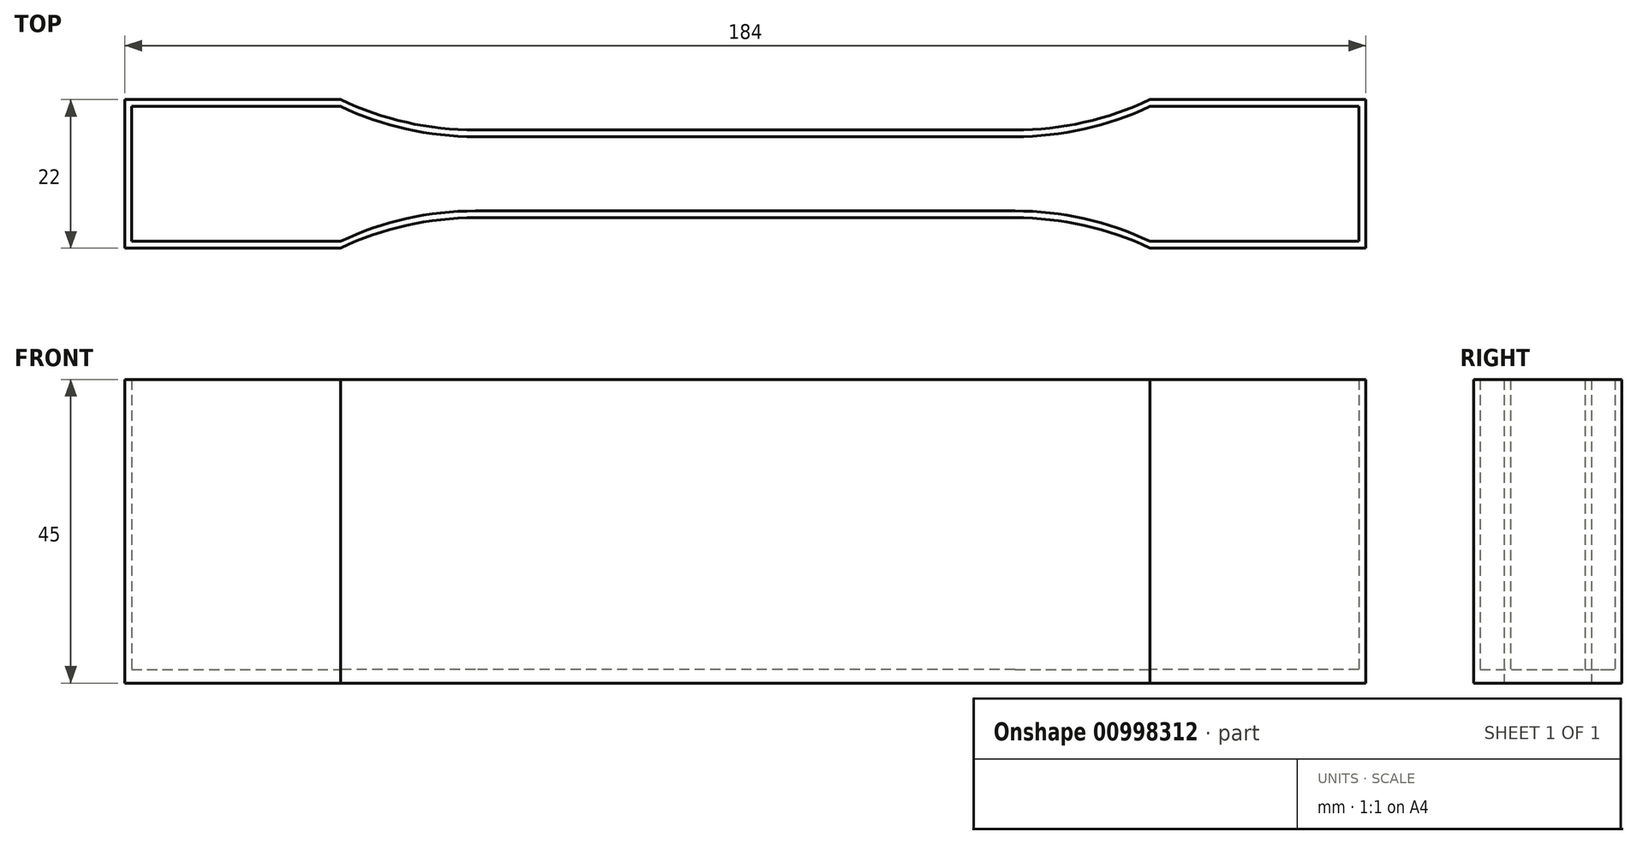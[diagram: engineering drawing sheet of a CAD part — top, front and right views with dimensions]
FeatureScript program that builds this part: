
annotation { "Feature Type Name" : "Feature", "Feature Type Description" : "" }
export const myFeature = defineFeature(function(context is Context, id is Id, definition is map)
    precondition{}
    {
        {
            var Q0;
            Q0=qCreatedBy(makeId("Top.planeOp"),FACE);
            var sketch = newSketch(context, id + "F0", { "sketchPlane" : qUnion([Q0])});
            skLineSegment(sketch, "E0", {"start": v(0, 0) * mm, "end": v(0, -20) * mm});
            skLineSegment(sketch, "E1", {"start": v(0, -20) * mm, "end": v(31, -20) * mm});
            skLineSegment(sketch, "E2", {"start": v(51, -15.5) * mm, "end": v(131, -15.5) * mm});
            skLineSegment(sketch, "E3", {"start": v(151, -20) * mm, "end": v(182, -20) * mm});
            skLineSegment(sketch, "E4", {"start": v(182, -20) * mm, "end": v(182, 0) * mm});
            skLineSegment(sketch, "E5", {"start": v(182, 0) * mm, "end": v(151, 0) * mm});
            skLineSegment(sketch, "E6", {"start": v(131, -4.5) * mm, "end": v(51, -4.5) * mm});
            skLineSegment(sketch, "E7", {"start": v(31, 0) * mm, "end": v(0, 0) * mm});
            skArc(sketch, "E8", {"start": v(31, 0) * mm, "mid": v(40.75, -3.36) * mm, "end": v(51, -4.5) * mm});
            skArc(sketch, "E9", {"start": v(51, -15.5) * mm, "mid": v(40.75, -16.64) * mm, "end": v(31, -20) * mm});
            skArc(sketch, "E10", {"start": v(131, -4.5) * mm, "mid": v(141.25, -3.36) * mm, "end": v(151, 0) * mm});
            skArc(sketch, "E11", {"start": v(151, -20) * mm, "mid": v(141.25, -16.64) * mm, "end": v(131, -15.5) * mm});
            skSolve(sketch);
        }
        {
            var Q0;
            Q0=makeQuery(id+"F0.imprint","IMPRINT",FACE,{"disambiguationData":[TD([[makeQuery(id+"F0.imprint","IMPRINT",EDGE,{"derivedFrom":sQuery(id+"F0.wireOp",EDGE,"E0")}),1.0]])]});
            var sketch = newSketch(context, id + "F1", { "sketchPlane" : qUnion([Q0])});
            skLineSegment(sketch, "E12", {"start": v(-1, 1) * mm, "end": v(-1, -21) * mm});
            skLineSegment(sketch, "E13", {"start": v(-1, -21) * mm, "end": v(31, -21) * mm});
            skLineSegment(sketch, "E14", {"start": v(51, -16.5) * mm, "end": v(131, -16.5) * mm});
            skLineSegment(sketch, "E15", {"start": v(151, -21) * mm, "end": v(183, -21) * mm});
            skLineSegment(sketch, "E16", {"start": v(183, -21) * mm, "end": v(183, 1) * mm});
            skLineSegment(sketch, "E17", {"start": v(183, 1) * mm, "end": v(151, 1) * mm});
            skLineSegment(sketch, "E18", {"start": v(-1, 1) * mm, "end": v(31, 1) * mm});
            skArc(sketch, "E19", {"start": v(151, -21) * mm, "mid": v(141.25, -17.64) * mm, "end": v(131, -16.5) * mm});
            skArc(sketch, "E20", {"start": v(51, -16.5) * mm, "mid": v(40.75, -17.64) * mm, "end": v(31, -21) * mm});
            skLineSegment(sketch, "E21", {"start": v(51, -3.5) * mm, "end": v(131, -3.5) * mm});
            skArc(sketch, "E22", {"start": v(31, 1) * mm, "mid": v(40.75, -2.36) * mm, "end": v(51, -3.5) * mm});
            skArc(sketch, "E23", {"start": v(131, -3.5) * mm, "mid": v(141.25, -2.36) * mm, "end": v(151, 1) * mm});
            skSolve(sketch);
        }
        {
            var Q0;
            Q0=makeQuery(id+"F1.imprint","IMPRINT",FACE,{"disambiguationData":[TD([[makeQuery(id+"F1.imprint","IMPRINT",EDGE,{"derivedFrom":sQuery(id+"F1.wireOp",EDGE,"E12")}),1.0]])]});
            extrude(context, id + "F2", {"entities" : qUnion([Q0]), "depth" : 45 * mm, "offsetDistance" : 25 * mm});
        }
        {
            var Q0;
            Q0=makeQuery(id+"F0.imprint","IMPRINT",FACE,{"disambiguationData":[TD([[makeQuery(id+"F0.imprint","IMPRINT",EDGE,{"derivedFrom":sQuery(id+"F0.wireOp",EDGE,"E0")}),1.0]])]});
            extrude(context, id + "F3", {"entities" : qUnion([Q0]), "operationType" : NewBodyOperationType.ADD, "depth" : 2 * mm, "offsetDistance" : 25 * mm});
        }
    });
